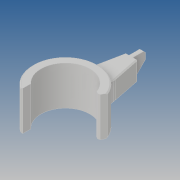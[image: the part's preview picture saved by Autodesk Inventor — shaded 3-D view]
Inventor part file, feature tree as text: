
AUTODESK INVENTOR PART (.ipt)
format: ipt  version: 2019 (Build 230136000, 136)  size: 177,152 bytes
history: native  units: mm
features: chamfer x6, other x4, extrude x1, sketch x1
ambient origin geometry x8: Origin, YZ Plane, XZ Plane, XY Plane, X Axis, Y Axis, Z Axis, Center Point
bodies: Body1 (feature_tree)
feature tree (12):
  other  "viseur_base.ipt"
  extrude  "Extrusion2"  Depth=10.0mm
  chamfer  "Chanfrein4"  Distance=12.0mm
  chamfer  "Chanfrein6"  Distance=2.0mm
  other  "Plan de construction1"
  chamfer  "Chanfrein11"  Distance=6.0mm
  chamfer  "Chanfrein12"  Distance=40.0mm
  chamfer  "Chanfrein13"  Distance=10.0mm
  chamfer  "Chanfrein14"  Distance=6.0mm Angle=45.0deg
  other  "Solide1::viseur_base.ipt"
  other  "FonctionRepérage1"
  sketch  "Esquisse2"
